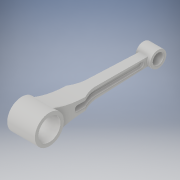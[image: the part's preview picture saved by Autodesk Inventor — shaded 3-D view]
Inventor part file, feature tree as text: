
AUTODESK INVENTOR PART (.ipt)
format: ipt  version: 2019 (Build 230136000, 136)  size: 195,584 bytes
history: native  units: mm
features: sketch x5, extrude x5, plane x2, loft x1, mirror x1, other x1
ambient origin geometry x8: Origin, YZ Plane, XZ Plane, XY Plane, X Axis, Y Axis, Z Axis, Center Point
bodies: Solid1 (feature_tree)
feature tree (15):
  sketch  "Sketch1"  dims[d16=3000.0mm d17=0.0mm d19=2100.0mm d20=0.0mm]
  extrude  "Extrusion1"  Depth=2100.0mm TaperAngle=0.0deg
  extrude  "Extrusion2"  Depth=900.0mm
  sketch  "Sketch5"  dims[d36=-11900.0mm d37=900.0mm]
  plane  "Work Plane3"
  sketch  "Sketch6"  dims[d38=900.0mm d50=0.0mm d51=90.0deg]
  loft  "Loft1"
  plane  "Work Plane6"
  extrude  "Extrusion4"  TaperAngle=0.0deg  [1 undecoded]
  extrude  "Extrusion5"  Depth=1600.0mm TaperAngle=0.0deg
  sketch  "Sketch11"  dims[d57=10000.0mm d58=0.0mm d59=1600.0mm d60=0.0mm d65=650.0mm d66=0.0mm d69=325.0mm d70=0.0mm]
  extrude  "Extrusion6"  Depth=650.0mm TaperAngle=0.0deg
  mirror  "Mirror2"
  other  "Edges1"
  sketch  "Sketch10"  dims[d52=0.0mm d53=90.0deg d54=0.0mm]
note: 1 required parameter value undecoded (feature->parameter linkage not recoverable at this tier; creation-order binding heuristic only, values carry confidence <= 0.55)
